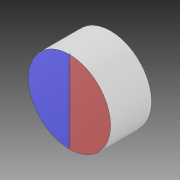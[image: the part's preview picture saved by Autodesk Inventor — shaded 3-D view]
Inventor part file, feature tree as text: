
AUTODESK INVENTOR PART (.ipt)
format: ipt  version: 2020 (Build 240168000, 168)  size: 105,472 bytes
history: native  units: mm
features: extrude x2, sketch x2
ambient origin geometry x8: Origin, YZ Plane, XZ Plane, XY Plane, X Axis, Y Axis, Z Axis, Center Point
bodies: Solid1 (feature_tree)
feature tree (4):
  extrude  "Extrusion1"  Depth=3.175mm TaperAngle=0.0deg
  extrude  "Extrusion2"  Depth=0.01mm
  sketch  "Sketch1"  dims[d0=6.35mm d1=3.175mm d2=0.0mm]
  sketch  "Sketch2"  dims[d3=8.818499mm d4=0.01mm d5=0.1mm d6=0.0mm]
